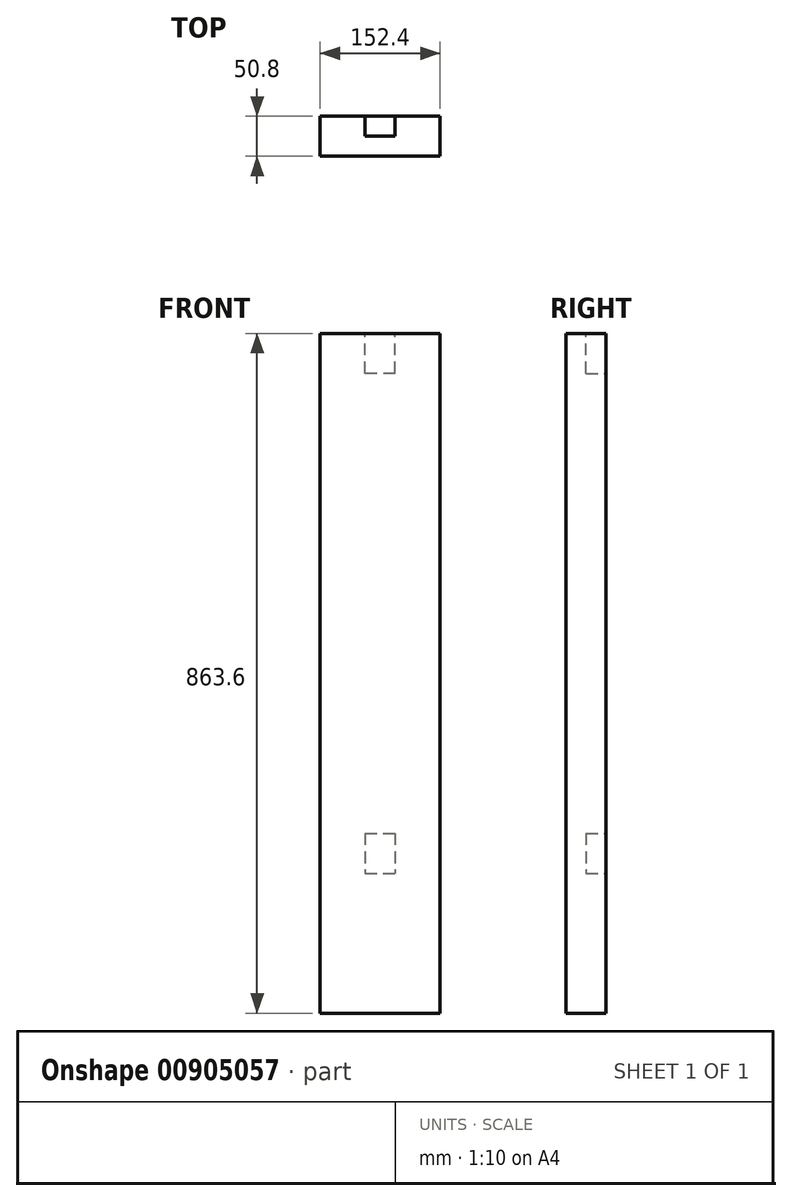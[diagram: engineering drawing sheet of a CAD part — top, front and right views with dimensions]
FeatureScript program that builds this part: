
annotation { "Feature Type Name" : "Feature", "Feature Type Description" : "" }
export const myFeature = defineFeature(function(context is Context, id is Id, definition is map)
    precondition{}
    {
        {
            var Q0;
            Q0=qCreatedBy(makeId("Top.planeOp"),FACE);
            var sketch = newSketch(context, id + "F0", { "sketchPlane" : qUnion([Q0])});
            skLineSegment(sketch, "E0.bottom", {"start": v(0, 0) * mm, "end": v(152.4, 0) * mm});
            skLineSegment(sketch, "E0.top", {"start": v(0, -50.8) * mm, "end": v(152.4, -50.8) * mm});
            skLineSegment(sketch, "E0.left", {"start": v(0, 0) * mm, "end": v(0, -50.8) * mm});
            skLineSegment(sketch, "E0.right", {"start": v(152.4, 0) * mm, "end": v(152.4, -50.8) * mm});
            skSolve(sketch);
        }
        {
            var Q0;
            Q0 = qSketchRegion(id + "F0", true);
            extrude(context, id + "F1", {"entities" : qUnion([Q0]), "depth" : 863.6 * mm, "offsetDistance" : 25.4 * mm});
        }
        {
            var Q0;
            Q0=makeQuery(id+"F1.opExtrude","SWEPT_FACE",FACE,{"disambiguationData":[OSD([sQuery(id+"F0.wireOp",EDGE,"E0.bottom")])]});
            var sketch = newSketch(context, id + "F2", { "sketchPlane" : qUnion([Q0])});
            skLineSegment(sketch, "E1", {"start": v(-76.2, 863.6) * mm, "end": v(-76.2, 838.2) * mm, "construction": true});
            skLineSegment(sketch, "E2.bottom", {"start": v(-95.25, 812.8) * mm, "end": v(-57.15, 812.8) * mm});
            skLineSegment(sketch, "E2.top", {"start": v(-95.25, 863.6) * mm, "end": v(-57.15, 863.6) * mm});
            skLineSegment(sketch, "E2.left", {"start": v(-95.25, 812.8) * mm, "end": v(-95.25, 863.6) * mm});
            skLineSegment(sketch, "E2.right", {"start": v(-57.15, 812.8) * mm, "end": v(-57.15, 863.6) * mm});
            skPoint(sketch, "E2.middle", {"position": v(-76.2, 838.2) * mm});
            skSolve(sketch);
        }
        {
            var Q0;
            Q0=makeQuery(id+"F2.imprint","IMPRINT",FACE,{"disambiguationData":[TD([[makeQuery(id+"F2.imprint","IMPRINT",EDGE,{"derivedFrom":sQuery(id+"F2.wireOp",EDGE,"E2.bottom")}),1.0]])]});
            extrude(context, id + "F3", {"entities" : qUnion([Q0]), "operationType" : NewBodyOperationType.REMOVE, "oppositeDirection" : true, "depth" : 25.4 * mm, "offsetDistance" : 25.4 * mm});
        }
        {
            var Q0;
            Q0=makeQuery(id+"F1.opExtrude","SWEPT_FACE",FACE,{"disambiguationData":[OSD([sQuery(id+"F0.wireOp",EDGE,"E0.bottom")])]});
            var sketch = newSketch(context, id + "F4", { "sketchPlane" : qUnion([Q0])});
            skLineSegment(sketch, "E3", {"start": v(-76.2, 0) * mm, "end": v(-76.2, 203.2) * mm, "construction": true});
            skLineSegment(sketch, "E4.bottom", {"start": v(-57.15, 228.6) * mm, "end": v(-95.25, 228.6) * mm});
            skLineSegment(sketch, "E4.top", {"start": v(-57.15, 177.8) * mm, "end": v(-95.25, 177.8) * mm});
            skLineSegment(sketch, "E4.left", {"start": v(-57.15, 228.6) * mm, "end": v(-57.15, 177.8) * mm});
            skLineSegment(sketch, "E4.right", {"start": v(-95.25, 228.6) * mm, "end": v(-95.25, 177.8) * mm});
            skPoint(sketch, "E4.middle", {"position": v(-76.2, 203.2) * mm});
            skSolve(sketch);
        }
        {
            var Q0;
            Q0=makeQuery(id+"F4.imprint","IMPRINT",FACE,{"disambiguationData":[TD([[makeQuery(id+"F4.imprint","IMPRINT",EDGE,{"derivedFrom":sQuery(id+"F4.wireOp",EDGE,"E4.bottom")}),1.0]])]});
            extrude(context, id + "F5", {"entities" : qUnion([Q0]), "operationType" : NewBodyOperationType.REMOVE, "oppositeDirection" : true, "depth" : 25.4 * mm, "offsetDistance" : 25.4 * mm});
        }
    });
